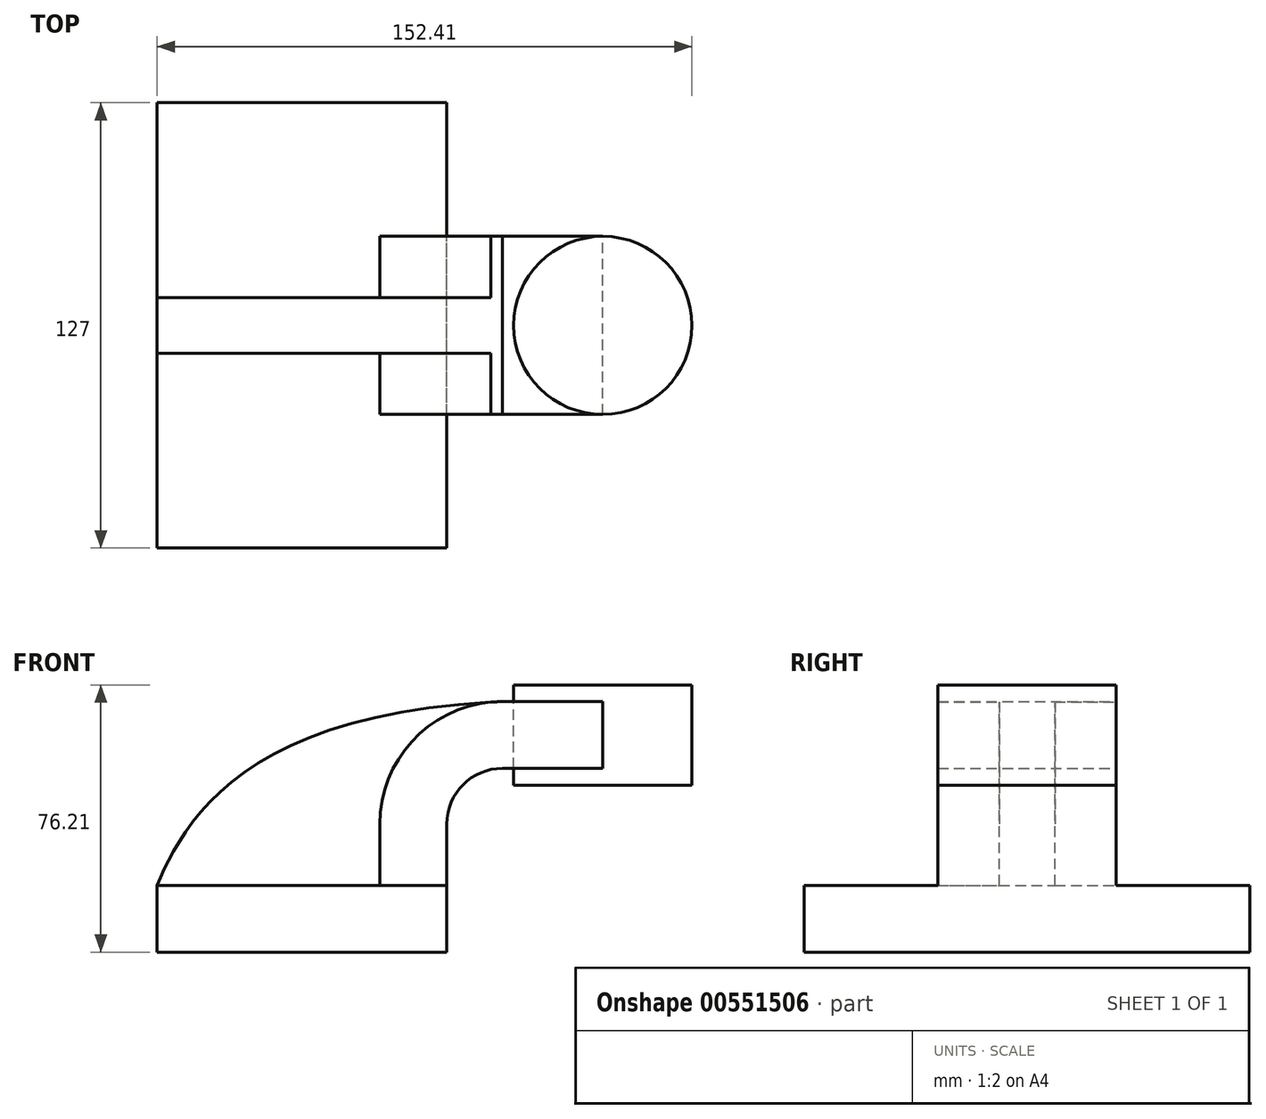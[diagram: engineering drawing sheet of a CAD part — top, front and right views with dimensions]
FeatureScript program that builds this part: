
annotation { "Feature Type Name" : "Feature", "Feature Type Description" : "" }
export const myFeature = defineFeature(function(context is Context, id is Id, definition is map)
    precondition{}
    {
        {
            var Q0;
            Q0=qCreatedBy(makeId("Front.planeOp"),FACE);
            var sketch = newSketch(context, id + "F0", { "sketchPlane" : qUnion([Q0])});
            skLineSegment(sketch, "E0.bottom", {"start": v(41.28, -9.53) * mm, "end": v(-41.28, -9.53) * mm});
            skLineSegment(sketch, "E0.top", {"start": v(41.28, 9.53) * mm, "end": v(-41.28, 9.53) * mm});
            skLineSegment(sketch, "E0.left", {"start": v(41.28, -9.53) * mm, "end": v(41.28, 9.53) * mm});
            skLineSegment(sketch, "E0.right", {"start": v(-41.28, -9.53) * mm, "end": v(-41.28, 9.53) * mm});
            skPoint(sketch, "E0.middle", {"position": v(0, 0) * mm});
            skLineSegment(sketch, "E1", {"start": v(41.28, 9.53) * mm, "end": v(41.28, 27) * mm});
            skLineSegment(sketch, "E2.bottom", {"start": v(60.32, 66.68) * mm, "end": v(111.12, 66.68) * mm});
            skLineSegment(sketch, "E2.top", {"start": v(60.32, 38.1) * mm, "end": v(111.12, 38.1) * mm});
            skLineSegment(sketch, "E2.left", {"start": v(60.32, 66.68) * mm, "end": v(60.32, 38.1) * mm});
            skLineSegment(sketch, "E2.right", {"start": v(111.12, 66.68) * mm, "end": v(111.12, 38.1) * mm});
            skPoint(sketch, "E2.middle", {"position": v(85.72, 52.39) * mm});
            skArc(sketch, "E3", {"start": v(41.27, 27) * mm, "mid": v(45.92, 38.23) * mm, "end": v(57.15, 42.88) * mm});
            skLineSegment(sketch, "E4", {"start": v(85.72, 66.68) * mm, "end": v(85.72, 38.1) * mm});
            skLineSegment(sketch, "E5", {"start": v(57.15, 42.88) * mm, "end": v(85.72, 42.88) * mm});
            skLineSegment(sketch, "E6.0", {"start": v(57.15, 61.93) * mm, "end": v(85.72, 61.93) * mm});
            skArc(sketch, "E6.1", {"start": v(22.23, 27) * mm, "mid": v(32.45, 51.7) * mm, "end": v(57.15, 61.93) * mm});
            skLineSegment(sketch, "E6.2", {"start": v(22.22, 9.53) * mm, "end": v(22.22, 27) * mm});
            skFitSpline(sketch, "E7", {"points": [v(-41.28, 9.52) * mm, v(57.15, 61.93) * mm], "startDerivative": vector(21.02, 49.94) * mm, "endDerivative": vector(225.71, 9.41) * mm});
            skSolve(sketch);
        }
        {
            var Q0;
            Q0=makeQuery(id+"F0.imprint","IMPRINT",FACE,{"disambiguationData":[TD([[makeQuery(id+"F0.imprint","IMPRINT",EDGE,{"derivedFrom":sQuery(id+"F0.wireOp",EDGE,"E0.bottom")}),-1.0]])]});
            extrude(context, id + "F1", {"entities" : qUnion([Q0]), "endBound" : BoundingType.SYMMETRIC, "depth" : 127 * mm, "offsetDistance" : 25.4 * mm});
        }
        {
            var Q0;
            {var subQ1=sQuery(id+"F0.wireOp",EDGE,"E1");Q0=makeQuery(id+"F0.imprint","IMPRINT",FACE,{"disambiguationData":[TD([[makeQuery(id+"F0.imprint","IMPRINT",EDGE,{"derivedFrom":subQ1}),1.0]])]});}
            var Q1;
            {var subQ0=sQuery(id+"F0.wireOp",EDGE,"E6.0");var subQ1=sQuery(id+"F0.wireOp",EDGE,"E2.left");var subQ2=makeQuery(id+"F0.imprint","INTERSECT",VERTEX,{"derivedFrom":[subQ1,subQ0]});Q1=makeQuery(id+"F0.imprint","IMPRINT",FACE,{"disambiguationData":[TD([[makeQuery(id+"F0.imprint","IMPRINT",EDGE,{"disambiguationData":[TD([[subQ2,-1.0]])],"derivedFrom":subQ1}),1.0]])]});}
            extrude(context, id + "F2", {"entities" : qUnion([Q0, Q1]), "operationType" : NewBodyOperationType.ADD, "endBound" : BoundingType.SYMMETRIC, "depth" : 50.8 * mm, "offsetDistance" : 25.4 * mm});
        }
        {
            var Q0;
            {var subQ3=sQuery(id+"F0.wireOp",EDGE,"E6.2");Q0=makeQuery(id+"F0.imprint","IMPRINT",FACE,{"disambiguationData":[TD([[makeQuery(id+"F0.imprint","IMPRINT",EDGE,{"derivedFrom":subQ3}),1.0]])]});}
            extrude(context, id + "F3", {"entities" : qUnion([Q0]), "operationType" : NewBodyOperationType.ADD, "endBound" : BoundingType.SYMMETRIC, "depth" : 15.88 * mm, "offsetDistance" : 25.4 * mm});
        }
        {
            var Q0;
            {var subQ4=sQuery(id+"F0.wireOp",EDGE,"E2.right");Q0=makeQuery(id+"F0.imprint","IMPRINT",FACE,{"disambiguationData":[TD([[makeQuery(id+"F0.imprint","IMPRINT",EDGE,{"derivedFrom":subQ4}),-1.0]])]});}
            var Q1;
            Q1=sQuery(id+"F0.wireOp",EDGE,"E4");
            revolve(context, id + "F4", {"entities" : qUnion([Q0]), "axis" : qUnion([Q1]), "revolveType" : RevolveType.FULL});
        }
    });
